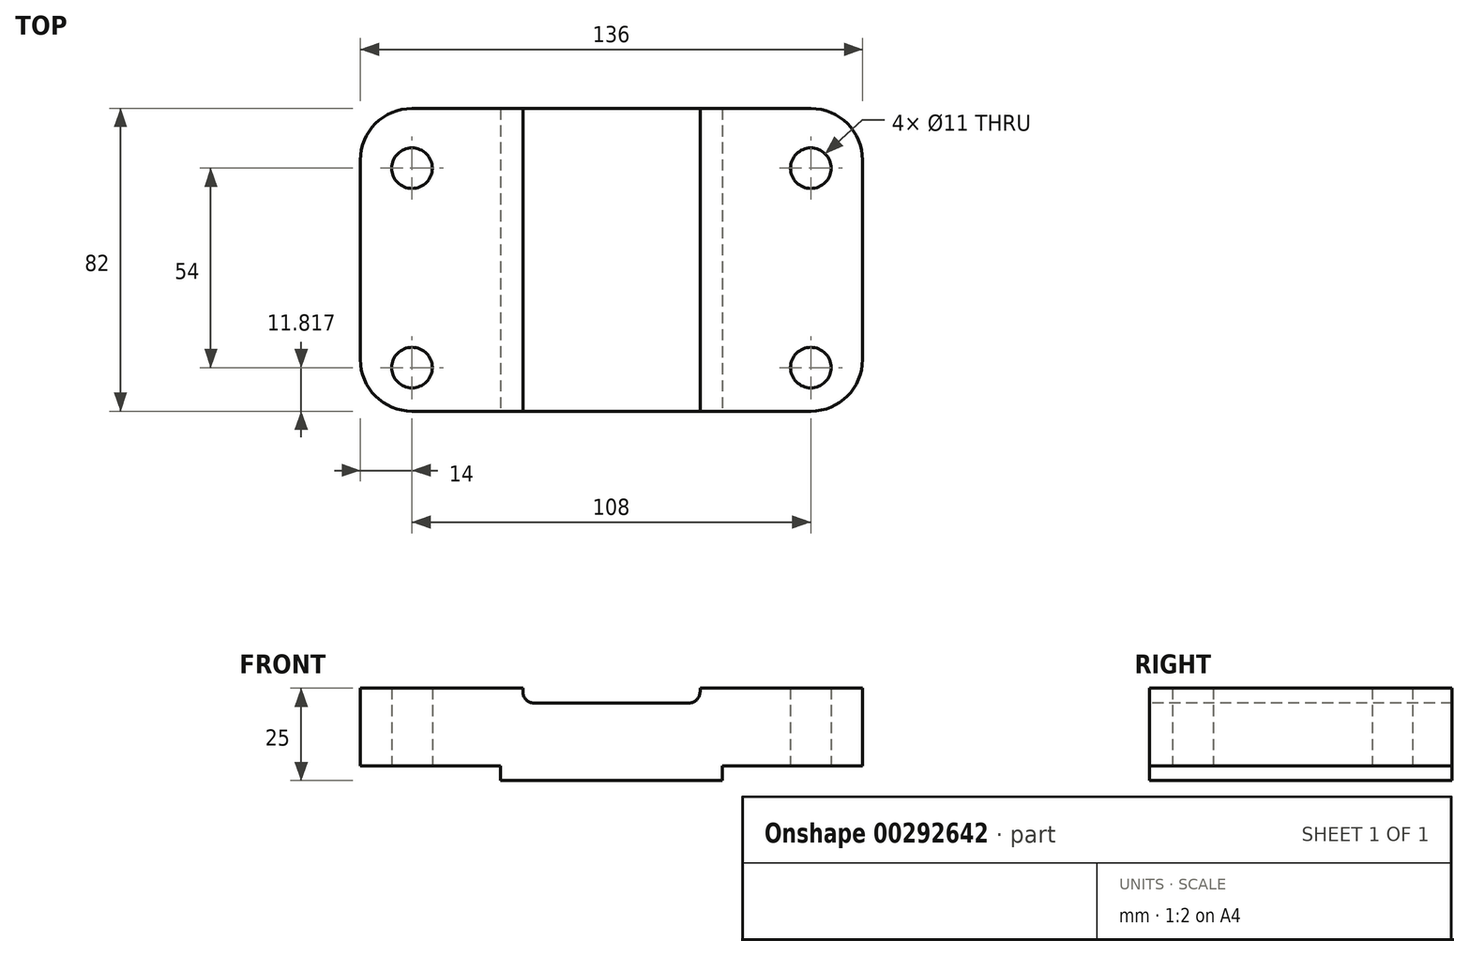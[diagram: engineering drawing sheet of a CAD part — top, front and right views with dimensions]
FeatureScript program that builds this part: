
annotation { "Feature Type Name" : "Feature", "Feature Type Description" : "" }
export const myFeature = defineFeature(function(context is Context, id is Id, definition is map)
    precondition{}
    {
        {
            var Q0;
            Q0=qCreatedBy(makeId("Top.planeOp"),FACE);
            var sketch = newSketch(context, id + "F0", { "sketchPlane" : qUnion([Q0])});
            skLineSegment(sketch, "E0", {"start": v(0, 0) * mm, "end": v(0, 82) * mm});
            skLineSegment(sketch, "E1", {"start": v(0, 82) * mm, "end": v(136, 82) * mm});
            skLineSegment(sketch, "E2", {"start": v(136, 82) * mm, "end": v(136, 0) * mm});
            skLineSegment(sketch, "E3", {"start": v(136, 0) * mm, "end": v(0, 0) * mm});
            skLineSegment(sketch, "E4", {"start": v(44, 82) * mm, "end": v(44, 0) * mm});
            skLineSegment(sketch, "E5", {"start": v(92, 82) * mm, "end": v(92, 0) * mm});
            skLineSegment(sketch, "E6.bottom", {"start": v(14, 65.82) * mm, "end": v(122, 65.82) * mm, "construction": true});
            skLineSegment(sketch, "E6.top", {"start": v(14, 11.82) * mm, "end": v(122, 11.82) * mm, "construction": true});
            skLineSegment(sketch, "E6.left", {"start": v(14, 65.82) * mm, "end": v(14, 11.82) * mm, "construction": true});
            skLineSegment(sketch, "E6.right", {"start": v(122, 65.82) * mm, "end": v(122, 11.82) * mm, "construction": true});
            skCircle(sketch, "E7", {"center": v(14, 65.82) * mm, "radius": 5.5 * mm});
            skCircle(sketch, "E8", {"center": v(122, 65.82) * mm, "radius": 5.5 * mm});
            skCircle(sketch, "E9", {"center": v(14, 11.82) * mm, "radius": 5.5 * mm});
            skCircle(sketch, "E10", {"center": v(122, 11.82) * mm, "radius": 5.5 * mm});
            skSolve(sketch);
        }
        {
            var Q0;
            Q0 = qSketchRegion(id + "F0", true);
            extrude(context, id + "F1", {"entities" : qUnion([Q0]), "depth" : 25 * mm, "symmetric" : true});
        }
        {
            var Q0;
            Q0=makeQuery(id+"F1.opExtrude","SWEPT_EDGE",EDGE,{"disambiguationData":[OSD([sQuery(id+"F0.wireOp",EDGE,"E0"),sQuery(id+"F0.wireOp",EDGE,"E1")])]});
            var Q1;
            Q1=makeQuery(id+"F1.opExtrude","SWEPT_EDGE",EDGE,{"disambiguationData":[OSD([sQuery(id+"F0.wireOp",EDGE,"E1"),sQuery(id+"F0.wireOp",EDGE,"E2")])]});
            var Q2;
            Q2=makeQuery(id+"F1.opExtrude","SWEPT_EDGE",EDGE,{"disambiguationData":[OSD([sQuery(id+"F0.wireOp",EDGE,"E2"),sQuery(id+"F0.wireOp",EDGE,"E3")])]});
            var Q3;
            Q3=makeQuery(id+"F1.opExtrude","SWEPT_EDGE",EDGE,{"disambiguationData":[OSD([sQuery(id+"F0.wireOp",EDGE,"E0"),sQuery(id+"F0.wireOp",EDGE,"E3")])]});
            fillet(context, id + "F2", {"entities" : qUnion([Q0, Q1, Q2, Q3]), "radius" : 14 * mm, "tangentPropagation" : true, "allowEdgeOverflow" : false});
        }
        {
            var Q0;
            Q0=makeQuery(id+"F1.opExtrude","SWEPT_FACE",FACE,{"disambiguationData":[OSD([sQuery(id+"F0.wireOp",EDGE,"E3")])]});
            var sketch = newSketch(context, id + "F3", { "sketchPlane" : qUnion([Q0])});
            skLineSegment(sketch, "E11", {"start": v(44, 12.5) * mm, "end": v(92, 12.5) * mm});
            skLineSegment(sketch, "E12", {"start": v(44, 8.5) * mm, "end": v(92, 8.5) * mm});
            skLineSegment(sketch, "E13", {"start": v(44, 12.5) * mm, "end": v(44, 8.5) * mm});
            skLineSegment(sketch, "E14", {"start": v(92, 12.5) * mm, "end": v(92, 8.5) * mm});
            skSolve(sketch);
        }
        {
            var Q0;
            Q0=makeQuery(id+"F3.imprint","IMPRINT",FACE,{"disambiguationData":[TD([[makeQuery(id+"F3.imprint","IMPRINT",EDGE,{"derivedFrom":sQuery(id+"F3.wireOp",EDGE,"E11")}),1.0]])]});
            extrude(context, id + "F4", {"entities" : qUnion([Q0]), "operationType" : NewBodyOperationType.REMOVE, "endBound" : BoundingType.THROUGH_ALL, "oppositeDirection" : true, "depth" : 25 * mm});
        }
        {
            var Q0;
            Q0=makeQuery(id+"F4.boolean.opBoolean","COPY",EDGE,{"derivedFrom":makeQuery(id+"F4.opExtrude","SWEPT_EDGE",EDGE,{"disambiguationData":[OSD([sQuery(id+"F3.wireOp",EDGE,"E12"),sQuery(id+"F3.wireOp",EDGE,"E13")])]})});
            var Q1;
            Q1=makeQuery(id+"F4.boolean.opBoolean","COPY",EDGE,{"derivedFrom":makeQuery(id+"F4.opExtrude","SWEPT_EDGE",EDGE,{"disambiguationData":[OSD([sQuery(id+"F3.wireOp",EDGE,"E12"),sQuery(id+"F3.wireOp",EDGE,"E14")])]})});
            fillet(context, id + "F5", {"entities" : qUnion([Q0, Q1]), "radius" : 3 * mm, "tangentPropagation" : true, "allowEdgeOverflow" : false});
        }
        {
            var Q0;
            Q0=makeQuery(id+"F1.opExtrude","SWEPT_FACE",FACE,{"disambiguationData":[OSD([sQuery(id+"F0.wireOp",EDGE,"E3")])]});
            var sketch = newSketch(context, id + "F6", { "sketchPlane" : qUnion([Q0])});
            skLineSegment(sketch, "E15", {"start": v(38, -12.5) * mm, "end": v(98, -12.5) * mm});
            skLineSegment(sketch, "E16", {"start": v(38, -12.5) * mm, "end": v(38, -8.5) * mm});
            skLineSegment(sketch, "E17", {"start": v(38, -8.5) * mm, "end": v(0, -8.5) * mm});
            skLineSegment(sketch, "E18", {"start": v(0, -8.5) * mm, "end": v(0, -12.5) * mm});
            skLineSegment(sketch, "E19", {"start": v(38, -12.5) * mm, "end": v(0, -12.5) * mm});
            skLineSegment(sketch, "E20", {"start": v(98, -12.5) * mm, "end": v(98, -8.5) * mm});
            skLineSegment(sketch, "E21", {"start": v(98, -8.5) * mm, "end": v(136, -8.5) * mm});
            skLineSegment(sketch, "E22", {"start": v(136, -8.5) * mm, "end": v(136, -12.5) * mm});
            skLineSegment(sketch, "E23", {"start": v(136, -12.5) * mm, "end": v(98, -12.5) * mm});
            skSolve(sketch);
        }
        {
            var Q0;
            Q0 = qSketchRegion(id + "F6", true);
            extrude(context, id + "F7", {"entities" : qUnion([Q0]), "operationType" : NewBodyOperationType.REMOVE, "endBound" : BoundingType.THROUGH_ALL, "oppositeDirection" : true, "depth" : 25 * mm});
        }
    });
